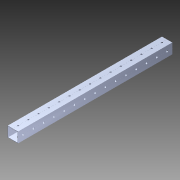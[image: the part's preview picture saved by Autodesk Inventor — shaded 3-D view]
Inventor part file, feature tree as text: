
AUTODESK INVENTOR PART (.ipt)
format: ipt  version: 2014 (Build 180170000, 170)  size: 1,158,656 bytes
history: native  units: in
note: dims shown in document units (in); Inventor stores cm internally (conversion verified against a paired STEP export)
features: pattern_circular x1, other x1, extrude x1, imported_body x1, sketch x1
ambient origin geometry x8: Origin, YZ Plane, XZ Plane, XY Plane, X Axis, Y Axis, Z Axis, Center Point
bodies: Body1 (feature_tree)
feature tree (5):
  pattern_circular  "CirPattern2"
  other  "1x1 tube1"
  extrude  "Extrusion1"  [1 undecoded]
  imported_body  "Base1"
  sketch  "Sketch1"  dims[d0=44.0in d1=0.0in]
note: 1 required parameter value undecoded (feature->parameter linkage not recoverable at this tier; creation-order binding heuristic only, values carry confidence <= 0.55)
